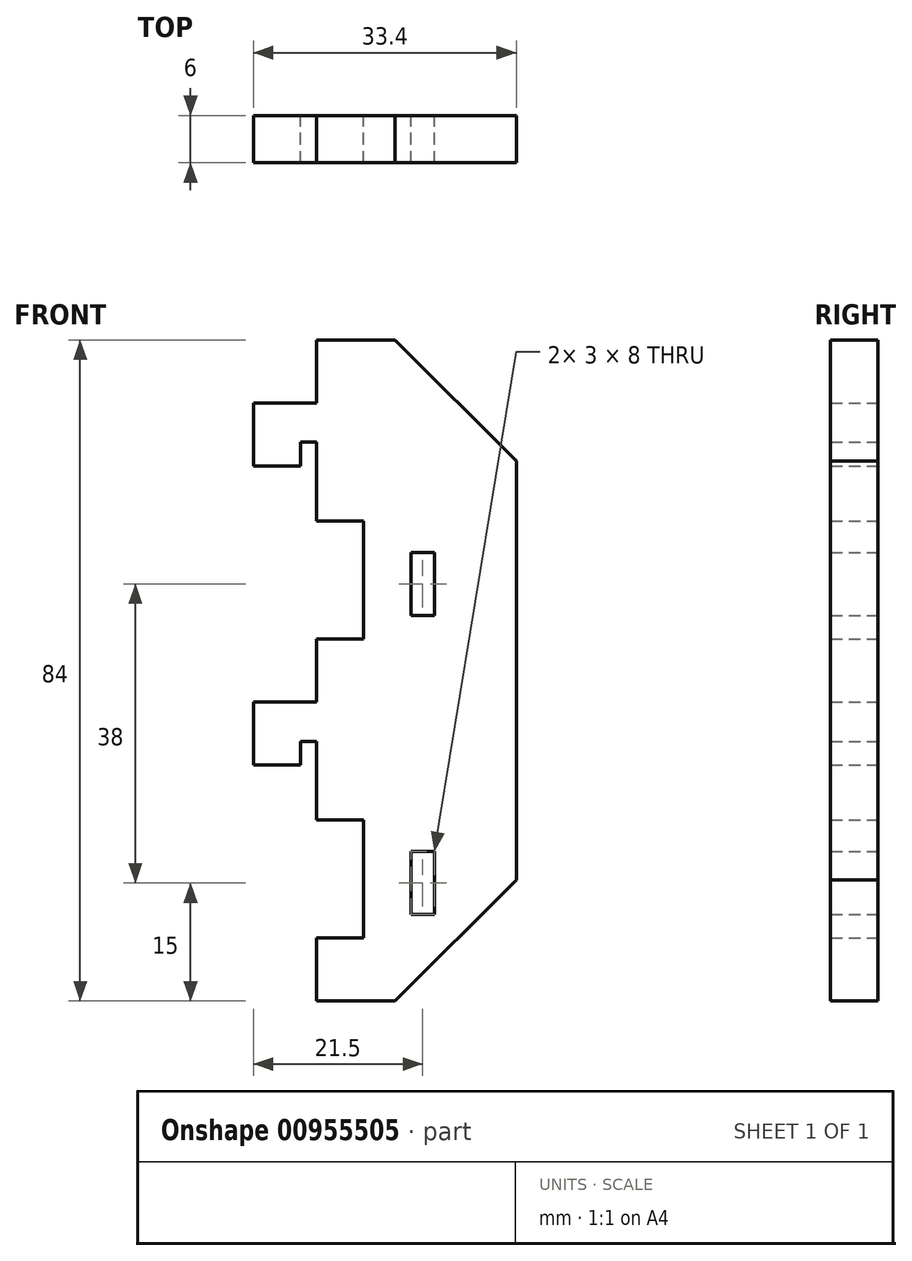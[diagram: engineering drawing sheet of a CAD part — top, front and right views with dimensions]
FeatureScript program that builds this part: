
annotation { "Feature Type Name" : "Feature", "Feature Type Description" : "" }
export const myFeature = defineFeature(function(context is Context, id is Id, definition is map)
    precondition{}
    {
        {
            var Q0;
            Q0=qCreatedBy(makeId("Front.planeOp"),FACE);
            var sketch = newSketch(context, id + "F0", { "sketchPlane" : qUnion([Q0])});
            skLineSegment(sketch, "E0", {"start": v(0, 38) * mm, "end": v(-8, 38) * mm});
            skLineSegment(sketch, "E1", {"start": v(-8, 38) * mm, "end": v(-8, 30) * mm});
            skLineSegment(sketch, "E2", {"start": v(-8, 30) * mm, "end": v(-2, 30) * mm});
            skLineSegment(sketch, "E3", {"start": v(-2, 30) * mm, "end": v(-2, 33) * mm});
            skLineSegment(sketch, "E4", {"start": v(-2, 33) * mm, "end": v(0, 33) * mm});
            skLineSegment(sketch, "E5", {"start": v(0, 33) * mm, "end": v(0, 23) * mm});
            skLineSegment(sketch, "E6.0.1.0", {"start": v(-8, 76) * mm, "end": v(-8, 68) * mm});
            skLineSegment(sketch, "E6.0.1.1", {"start": v(0, 76) * mm, "end": v(-8, 76) * mm});
            skLineSegment(sketch, "E6.0.1.2", {"start": v(-8, 68) * mm, "end": v(-2, 68) * mm});
            skLineSegment(sketch, "E6.0.1.3", {"start": v(-2, 68) * mm, "end": v(-2, 71) * mm});
            skLineSegment(sketch, "E6.0.1.4", {"start": v(-2, 71) * mm, "end": v(0, 71) * mm});
            skLineSegment(sketch, "E6.0.1.5", {"start": v(0, 71) * mm, "end": v(0, 61) * mm});
            skLineSegment(sketch, "E6.0.2.0", {"start": v(-8, 114) * mm, "end": v(-8, 106) * mm});
            skLineSegment(sketch, "E6.0.2.1", {"start": v(0, 114) * mm, "end": v(-8, 114) * mm});
            skLineSegment(sketch, "E6.0.2.2", {"start": v(-8, 106) * mm, "end": v(-2, 106) * mm});
            skLineSegment(sketch, "E6.0.2.3", {"start": v(-2, 106) * mm, "end": v(-2, 109) * mm});
            skLineSegment(sketch, "E6.0.2.4", {"start": v(-2, 109) * mm, "end": v(0, 109) * mm});
            skLineSegment(sketch, "E6.0.2.5", {"start": v(0, 109) * mm, "end": v(0, 99) * mm});
            skLineSegment(sketch, "E6.direction1", {"start": v(-8, 30) * mm, "end": v(17, 30) * mm, "construction": true});
            skLineSegment(sketch, "E6.direction2", {"start": v(-8, 30) * mm, "end": v(-8, 68) * mm, "construction": true});
            skPoint(sketch, "E7.orphan", {"position": v(0, 76) * mm});
            skLineSegment(sketch, "E8", {"start": v(0, 114) * mm, "end": v(0, 122) * mm});
            skLineSegment(sketch, "E9", {"start": v(0, 122) * mm, "end": v(10, 122) * mm});
            skLineSegment(sketch, "E10", {"start": v(10, 122) * mm, "end": v(25.4, 106.6) * mm});
            skLineSegment(sketch, "E11", {"start": v(25.4, 106.6) * mm, "end": v(25.4, 15.4) * mm});
            skLineSegment(sketch, "E12", {"start": v(25.4, 15.4) * mm, "end": v(10, 0) * mm});
            skLineSegment(sketch, "E13", {"start": v(10, 0) * mm, "end": v(0, 0) * mm});
            skLineSegment(sketch, "E14.bottom", {"start": v(0, 99) * mm, "end": v(6, 99) * mm});
            skLineSegment(sketch, "E14.top", {"start": v(0, 84) * mm, "end": v(6, 84) * mm});
            skLineSegment(sketch, "E14.right", {"start": v(6, 99) * mm, "end": v(6, 84) * mm});
            skLineSegment(sketch, "E15.trimOffspring", {"start": v(0, 84) * mm, "end": v(0, 76) * mm});
            skLineSegment(sketch, "E16.0.1.0", {"start": v(0, 61) * mm, "end": v(6, 61) * mm});
            skLineSegment(sketch, "E16.0.1.1", {"start": v(6, 61) * mm, "end": v(6, 46) * mm});
            skLineSegment(sketch, "E16.0.1.2", {"start": v(0, 46) * mm, "end": v(6, 46) * mm});
            skLineSegment(sketch, "E16.0.2.0", {"start": v(0, 23) * mm, "end": v(6, 23) * mm});
            skLineSegment(sketch, "E16.0.2.1", {"start": v(6, 23) * mm, "end": v(6, 8) * mm});
            skLineSegment(sketch, "E16.0.2.2", {"start": v(0, 8) * mm, "end": v(6, 8) * mm});
            skLineSegment(sketch, "E16.direction1", {"start": v(0, 99) * mm, "end": v(25, 99) * mm, "construction": true});
            skLineSegment(sketch, "E16.direction2", {"start": v(0, 99) * mm, "end": v(0, 61) * mm, "construction": true});
            skLineSegment(sketch, "E17.trimOffspring", {"start": v(0, 46) * mm, "end": v(0, 38) * mm});
            skLineSegment(sketch, "E18.trimOffspring", {"start": v(0, 8) * mm, "end": v(0, 0) * mm});
            skLineSegment(sketch, "E19.bottom", {"start": v(12, 49) * mm, "end": v(15, 49) * mm});
            skLineSegment(sketch, "E19.top", {"start": v(12, 57) * mm, "end": v(15, 57) * mm});
            skLineSegment(sketch, "E19.left", {"start": v(12, 49) * mm, "end": v(12, 57) * mm});
            skLineSegment(sketch, "E19.right", {"start": v(15, 49) * mm, "end": v(15, 57) * mm});
            skLineSegment(sketch, "E20.0.1.0", {"start": v(12, 11) * mm, "end": v(12, 19) * mm});
            skLineSegment(sketch, "E20.0.1.1", {"start": v(12, 19) * mm, "end": v(15, 19) * mm});
            skLineSegment(sketch, "E20.0.1.2", {"start": v(15, 11) * mm, "end": v(15, 19) * mm});
            skLineSegment(sketch, "E20.0.1.3", {"start": v(12, 11) * mm, "end": v(15, 11) * mm});
            skLineSegment(sketch, "E20.direction1", {"start": v(12, 49) * mm, "end": v(37, 49) * mm, "construction": true});
            skLineSegment(sketch, "E20.direction2", {"start": v(12, 49) * mm, "end": v(12, 11) * mm, "construction": true});
            skSolve(sketch);
        }
        {
            var Q0;
            Q0=makeQuery(id+"F0.imprint","IMPRINT",FACE,{"disambiguationData":[TD([[makeQuery(id+"F0.imprint","IMPRINT",EDGE,{"derivedFrom":sQuery(id+"F0.wireOp",EDGE,"E0")}),1.0]])]});
            extrude(context, id + "F1", {"entities" : qUnion([Q0]), "depth" : 6 * mm, "offsetDistance" : 25 * mm});
        }
        {
            var Q0;
            Q0=makeQuery(id+"F1.opExtrude","CAP_FACE",FACE,{"disambiguationData":[OSD([sQuery(id+"F0.wireOp",EDGE,"E0"),sQuery(id+"F0.wireOp",EDGE,"E1"),sQuery(id+"F0.wireOp",EDGE,"E2"),sQuery(id+"F0.wireOp",EDGE,"E3"),sQuery(id+"F0.wireOp",EDGE,"E4"),sQuery(id+"F0.wireOp",EDGE,"E5"),sQuery(id+"F0.wireOp",EDGE,"E6.0.1.0"),sQuery(id+"F0.wireOp",EDGE,"E6.0.1.1"),sQuery(id+"F0.wireOp",EDGE,"E6.0.1.2"),sQuery(id+"F0.wireOp",EDGE,"E6.0.1.3"),sQuery(id+"F0.wireOp",EDGE,"E6.0.1.4"),sQuery(id+"F0.wireOp",EDGE,"E6.0.1.5"),sQuery(id+"F0.wireOp",EDGE,"E6.0.2.0"),sQuery(id+"F0.wireOp",EDGE,"E6.0.2.1"),sQuery(id+"F0.wireOp",EDGE,"E6.0.2.2"),sQuery(id+"F0.wireOp",EDGE,"E6.0.2.3"),sQuery(id+"F0.wireOp",EDGE,"E6.0.2.4"),sQuery(id+"F0.wireOp",EDGE,"E6.0.2.5"),sQuery(id+"F0.wireOp",EDGE,"E8"),sQuery(id+"F0.wireOp",EDGE,"E9"),sQuery(id+"F0.wireOp",EDGE,"E10"),sQuery(id+"F0.wireOp",EDGE,"E11"),sQuery(id+"F0.wireOp",EDGE,"E12"),sQuery(id+"F0.wireOp",EDGE,"E13"),sQuery(id+"F0.wireOp",EDGE,"E14.bottom"),sQuery(id+"F0.wireOp",EDGE,"E14.top"),sQuery(id+"F0.wireOp",EDGE,"E14.right"),sQuery(id+"F0.wireOp",EDGE,"E15.trimOffspring"),sQuery(id+"F0.wireOp",EDGE,"E16.0.1.0"),sQuery(id+"F0.wireOp",EDGE,"E16.0.1.1"),sQuery(id+"F0.wireOp",EDGE,"E16.0.1.2"),sQuery(id+"F0.wireOp",EDGE,"E16.0.2.0"),sQuery(id+"F0.wireOp",EDGE,"E16.0.2.1"),sQuery(id+"F0.wireOp",EDGE,"E16.0.2.2"),sQuery(id+"F0.wireOp",EDGE,"E17.trimOffspring"),sQuery(id+"F0.wireOp",EDGE,"E18.trimOffspring")])],"isStart":false});
            var sketch = newSketch(context, id + "F2", { "sketchPlane" : qUnion([Q0])});
            skLineSegment(sketch, "E21", {"start": v(0, 84) * mm, "end": v(10, 84) * mm});
            skLineSegment(sketch, "E22", {"start": v(10, 84) * mm, "end": v(25.4, 68.6) * mm});
            skLineSegment(sketch, "E23", {"start": v(25.4, 68.6) * mm, "end": v(32.79, 68.6) * mm});
            skLineSegment(sketch, "E24", {"start": v(32.79, 68.6) * mm, "end": v(32.79, 127.55) * mm});
            skLineSegment(sketch, "E25", {"start": v(32.79, 127.55) * mm, "end": v(-15.52, 123.84) * mm});
            skLineSegment(sketch, "E26", {"start": v(-15.52, 123.84) * mm, "end": v(-15.52, 88.45) * mm});
            skLineSegment(sketch, "E27", {"start": v(-15.52, 88.45) * mm, "end": v(0, 84) * mm});
            skSolve(sketch);
        }
        {
            var Q0;
            Q0 = qSketchRegion(id + "F2", true);
            extrude(context, id + "F3", {"entities" : qUnion([Q0]), "operationType" : NewBodyOperationType.REMOVE, "oppositeDirection" : true, "depth" : 25 * mm, "offsetDistance" : 25 * mm});
        }
    });
